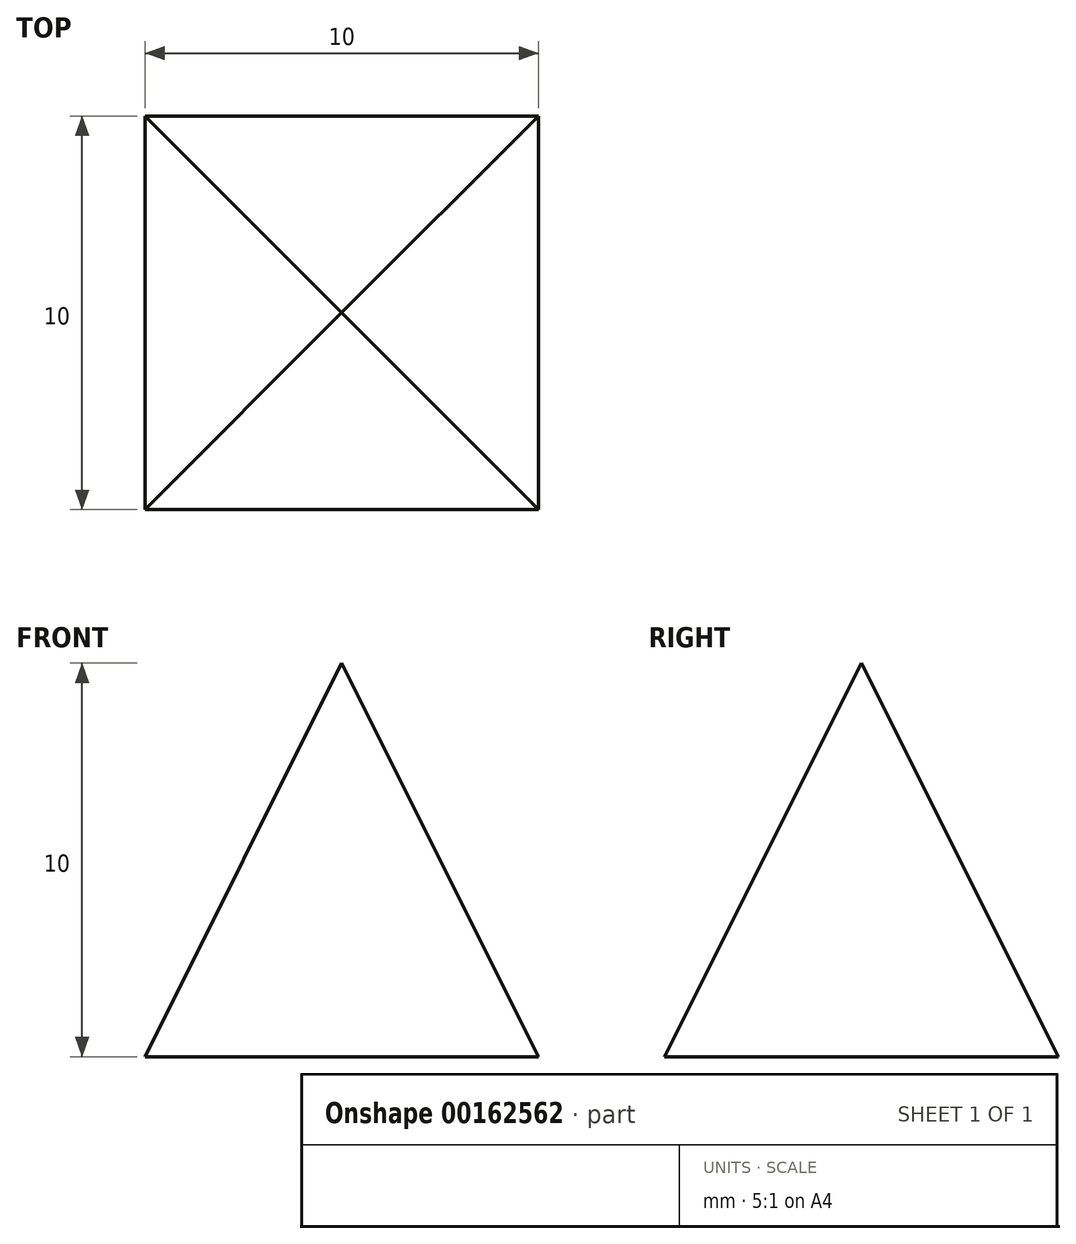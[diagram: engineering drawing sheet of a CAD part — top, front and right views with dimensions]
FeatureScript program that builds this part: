
annotation { "Feature Type Name" : "Feature", "Feature Type Description" : "" }
export const myFeature = defineFeature(function(context is Context, id is Id, definition is map)
    precondition{}
    {
        {
            var Q0;
            Q0=qCreatedBy(makeId("Top.planeOp"),FACE);
            var sketch = newSketch(context, id + "F0", { "sketchPlane" : qUnion([Q0])});
            skLineSegment(sketch, "E0.bottom", {"start": v(5, 5) * mm, "end": v(-5, 5) * mm});
            skLineSegment(sketch, "E0.top", {"start": v(5, -5) * mm, "end": v(-5, -5) * mm});
            skLineSegment(sketch, "E0.left", {"start": v(5, 5) * mm, "end": v(5, -5) * mm});
            skLineSegment(sketch, "E0.right", {"start": v(-5, 5) * mm, "end": v(-5, -5) * mm});
            skPoint(sketch, "E0.middle", {"position": v(0, 0) * mm});
            skSolve(sketch);
        }
        {
            var Q0;
            Q0=qCreatedBy(makeId("Top.planeOp"),FACE);
            cPlane(context, id + "F1", {"entities" : qUnion([Q0]), "cplaneType" : CPlaneType.OFFSET, "offset" : 10 * mm, "width" : 150 * mm, "height" : 150 * mm});
        }
        {
            var Q0;
            Q0=qCreatedBy(id+"F1.planeOp",FACE);
            var sketch = newSketch(context, id + "F2", { "sketchPlane" : qUnion([Q0])});
            skPoint(sketch, "E1", {"position": v(0, 0) * mm});
            skSolve(sketch);
        }
        {
            var Q0;
            Q0=sQuery(id+"F0.wireOp",VERTEX,"E0.left.end");
            var Q1;
            Q1=sQuery(id+"F2.wireOp",VERTEX,"E1");
            var Q2;
            Q2=sQuery(id+"F0.wireOp",VERTEX,"E0.bottom.start");
            cPlane(context, id + "F3", {"entities" : qUnion([Q0, Q1, Q2]), "cplaneType" : CPlaneType.THREE_POINT, "offset" : 25 * mm, "width" : 150 * mm, "height" : 150 * mm});
        }
        {
            var Q0;
            Q0=qCreatedBy(id+"F3.planeOp",FACE);
            var sketch = newSketch(context, id + "F4", { "sketchPlane" : qUnion([Q0])});
            skLineSegment(sketch, "E2", {"start": v(-5, -2.24) * mm, "end": v(0, 8.94) * mm});
            skLineSegment(sketch, "E3", {"start": v(0, 8.94) * mm, "end": v(5, -2.24) * mm});
            skLineSegment(sketch, "E4", {"start": v(5, -2.24) * mm, "end": v(-5, -2.24) * mm});
            skSolve(sketch);
        }
        {
            var Q0;
            Q0=sQuery(id+"F0.wireOp",VERTEX,"E0.right.start");
            var Q1;
            Q1=sQuery(id+"F0.wireOp",VERTEX,"E0.right.end");
            var Q2;
            Q2=sQuery(id+"F2.wireOp",VERTEX,"E1");
            cPlane(context, id + "F5", {"entities" : qUnion([Q0, Q1, Q2]), "cplaneType" : CPlaneType.THREE_POINT, "offset" : 25 * mm, "width" : 150 * mm, "height" : 150 * mm});
        }
        {
            var Q0;
            Q0=qCreatedBy(id+"F5.planeOp",FACE);
            var sketch = newSketch(context, id + "F6", { "sketchPlane" : qUnion([Q0])});
            skLineSegment(sketch, "E5", {"start": v(5, -2.24) * mm, "end": v(0, 8.94) * mm});
            skLineSegment(sketch, "E6", {"start": v(0, 8.94) * mm, "end": v(-5, -2.24) * mm});
            skLineSegment(sketch, "E7", {"start": v(5, -2.24) * mm, "end": v(-5, -2.24) * mm});
            skSolve(sketch);
        }
        {
            var Q0;
            Q0 = qSketchRegion(id + "F0", true);
            extrude(context, id + "F7", {"entities" : qUnion([Q0]), "depth" : 10 * mm});
        }
        {
            var Q0;
            Q0 = qSketchRegion(id + "F4", true);
            extrude(context, id + "F8", {"entities" : qUnion([Q0]), "operationType" : NewBodyOperationType.REMOVE, "endBound" : BoundingType.THROUGH_ALL, "depth" : 25 * mm});
        }
        {
            var Q0;
            Q0 = qSketchRegion(id + "F6", true);
            extrude(context, id + "F9", {"entities" : qUnion([Q0]), "operationType" : NewBodyOperationType.REMOVE, "endBound" : BoundingType.THROUGH_ALL, "oppositeDirection" : true, "depth" : 25 * mm});
        }
        {
            var Q0;
            Q0=sQuery(id+"F2.wireOp",VERTEX,"E1");
            var Q1;
            Q1=makeQuery(id+"F9.boolean.opBoolean","MERGE",VERTEX,{"derivedFrom":[makeQuery(id+"F7.opExtrude","CAP_VERTEX",VERTEX,{"disambiguationData":[OSD([sQuery(id+"F0.wireOp",EDGE,"E0.top"),sQuery(id+"F0.wireOp",EDGE,"E0.right")])],"isStart":true}),makeQuery(id+"F9.opExtrude","CAP_VERTEX",VERTEX,{"disambiguationData":[OSD([sQuery(id+"F6.wireOp",EDGE,"E6"),sQuery(id+"F6.wireOp",EDGE,"E7")])],"isStart":true})]});
            var Q2;
            Q2=makeQuery(id+"F8.boolean.opBoolean","MERGE",VERTEX,{"derivedFrom":[makeQuery(id+"F7.opExtrude","CAP_VERTEX",VERTEX,{"disambiguationData":[OSD([sQuery(id+"F0.wireOp",EDGE,"E0.top"),sQuery(id+"F0.wireOp",EDGE,"E0.left")])],"isStart":true}),makeQuery(id+"F8.opExtrude","CAP_VERTEX",VERTEX,{"disambiguationData":[OSD([sQuery(id+"F4.wireOp",EDGE,"E2"),sQuery(id+"F4.wireOp",EDGE,"E4")])],"isStart":true})]});
            cPlane(context, id + "F10", {"entities" : qUnion([Q0, Q1, Q2]), "cplaneType" : CPlaneType.THREE_POINT, "offset" : 25 * mm, "width" : 150 * mm, "height" : 150 * mm});
        }
        {
            var Q0;
            Q0=sQuery(id+"F2.wireOp",VERTEX,"E1");
            var Q1;
            Q1=makeQuery(id+"F9.boolean.opBoolean","MERGE",VERTEX,{"derivedFrom":[makeQuery(id+"F7.opExtrude","CAP_VERTEX",VERTEX,{"disambiguationData":[OSD([sQuery(id+"F0.wireOp",EDGE,"E0.bottom"),sQuery(id+"F0.wireOp",EDGE,"E0.right")])],"isStart":true}),makeQuery(id+"F9.opExtrude","CAP_VERTEX",VERTEX,{"disambiguationData":[OSD([sQuery(id+"F6.wireOp",EDGE,"E5"),sQuery(id+"F6.wireOp",EDGE,"E7")])],"isStart":true})]});
            var Q2;
            Q2=makeQuery(id+"F8.boolean.opBoolean","MERGE",VERTEX,{"derivedFrom":[makeQuery(id+"F7.opExtrude","CAP_VERTEX",VERTEX,{"disambiguationData":[OSD([sQuery(id+"F0.wireOp",EDGE,"E0.bottom"),sQuery(id+"F0.wireOp",EDGE,"E0.left")])],"isStart":true}),makeQuery(id+"F8.opExtrude","CAP_VERTEX",VERTEX,{"disambiguationData":[OSD([sQuery(id+"F4.wireOp",EDGE,"E3"),sQuery(id+"F4.wireOp",EDGE,"E4")])],"isStart":true})]});
            cPlane(context, id + "F11", {"entities" : qUnion([Q0, Q1, Q2]), "cplaneType" : CPlaneType.THREE_POINT, "offset" : 25 * mm, "width" : 150 * mm, "height" : 150 * mm});
        }
        {
            var Q0;
            Q0=qCreatedBy(id+"F10.planeOp",FACE);
            var sketch = newSketch(context, id + "F12", { "sketchPlane" : qUnion([Q0])});
            skLineSegment(sketch, "E8.bottom", {"start": v(-9.04, -7.62) * mm, "end": v(10.26, -7.62) * mm});
            skLineSegment(sketch, "E8.top", {"start": v(-9.04, 11.25) * mm, "end": v(10.26, 11.25) * mm});
            skLineSegment(sketch, "E8.left", {"start": v(-9.04, -7.62) * mm, "end": v(-9.04, 11.25) * mm});
            skLineSegment(sketch, "E8.right", {"start": v(10.26, -7.62) * mm, "end": v(10.26, 11.25) * mm});
            skSolve(sketch);
        }
        {
            var Q0;
            Q0 = qSketchRegion(id + "F12", true);
            extrude(context, id + "F13", {"entities" : qUnion([Q0]), "operationType" : NewBodyOperationType.REMOVE, "endBound" : BoundingType.THROUGH_ALL, "oppositeDirection" : true, "depth" : 25 * mm});
        }
        {
            var Q0;
            Q0=qCreatedBy(id+"F11.planeOp",FACE);
            var sketch = newSketch(context, id + "F14", { "sketchPlane" : qUnion([Q0])});
            skLineSegment(sketch, "E9.bottom", {"start": v(-25.95, -19) * mm, "end": v(22.3, -19) * mm});
            skLineSegment(sketch, "E9.top", {"start": v(-25.95, 24.7) * mm, "end": v(22.3, 24.7) * mm});
            skLineSegment(sketch, "E9.left", {"start": v(-25.95, -19) * mm, "end": v(-25.95, 24.7) * mm});
            skLineSegment(sketch, "E9.right", {"start": v(22.3, -19) * mm, "end": v(22.3, 24.7) * mm});
            skSolve(sketch);
        }
        {
            var Q0;
            Q0 = qSketchRegion(id + "F14", true);
            extrude(context, id + "F15", {"entities" : qUnion([Q0]), "operationType" : NewBodyOperationType.REMOVE, "endBound" : BoundingType.THROUGH_ALL, "depth" : 25 * mm});
        }
    });
